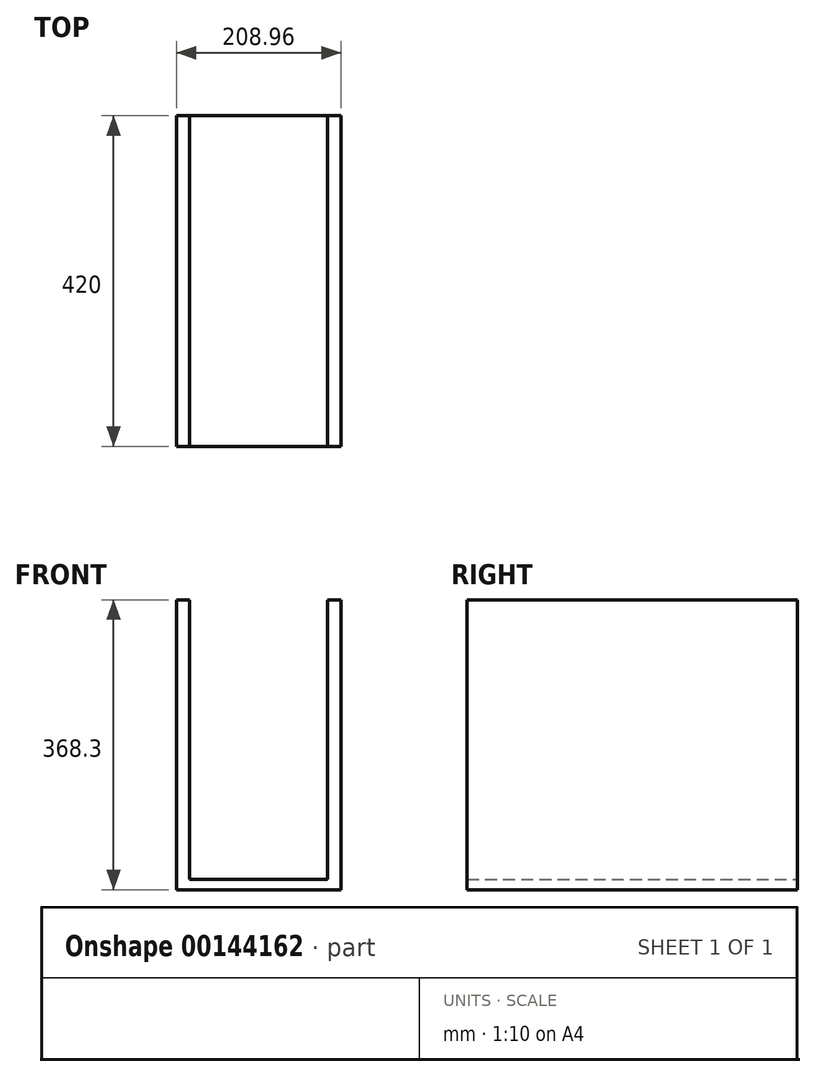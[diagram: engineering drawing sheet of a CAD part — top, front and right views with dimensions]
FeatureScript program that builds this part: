
annotation { "Feature Type Name" : "Feature", "Feature Type Description" : "" }
export const myFeature = defineFeature(function(context is Context, id is Id, definition is map)
    precondition{}
    {
        {
            var Q0;
            Q0=qCreatedBy(makeId("Front.planeOp"),FACE);
            var sketch = newSketch(context, id + "F0", { "sketchPlane" : qUnion([Q0])});
            skLineSegment(sketch, "E0", {"start": v(0, 0) * mm, "end": v(208.96, 0) * mm});
            skLineSegment(sketch, "E1", {"start": v(208.96, 0) * mm, "end": v(208.96, 368.3) * mm});
            skLineSegment(sketch, "E2", {"start": v(208.96, 368.3) * mm, "end": v(191.55, 368.3) * mm});
            skLineSegment(sketch, "E3", {"start": v(191.55, 368.3) * mm, "end": v(191.55, 13.3) * mm});
            skLineSegment(sketch, "E4", {"start": v(0, 0) * mm, "end": v(0, 368.3) * mm});
            skLineSegment(sketch, "E5", {"start": v(0, 368.3) * mm, "end": v(16.55, 368.3) * mm});
            skLineSegment(sketch, "E6", {"start": v(16.55, 368.3) * mm, "end": v(16.55, 13.3) * mm});
            skLineSegment(sketch, "E7", {"start": v(16.55, 13.3) * mm, "end": v(191.55, 13.3) * mm});
            skPoint(sketch, "E8.orphan", {"position": v(191.55, -51.48) * mm});
            skSolve(sketch);
        }
        {
            var Q0;
            Q0=makeQuery(id+"F0.imprint","IMPRINT",FACE,{"disambiguationData":[TD([[makeQuery(id+"F0.imprint","IMPRINT",EDGE,{"derivedFrom":sQuery(id+"F0.wireOp",EDGE,"E0")}),1.0]])]});
            extrude(context, id + "F1", {"entities" : qUnion([Q0]), "depth" : 420 * mm});
        }
    });
